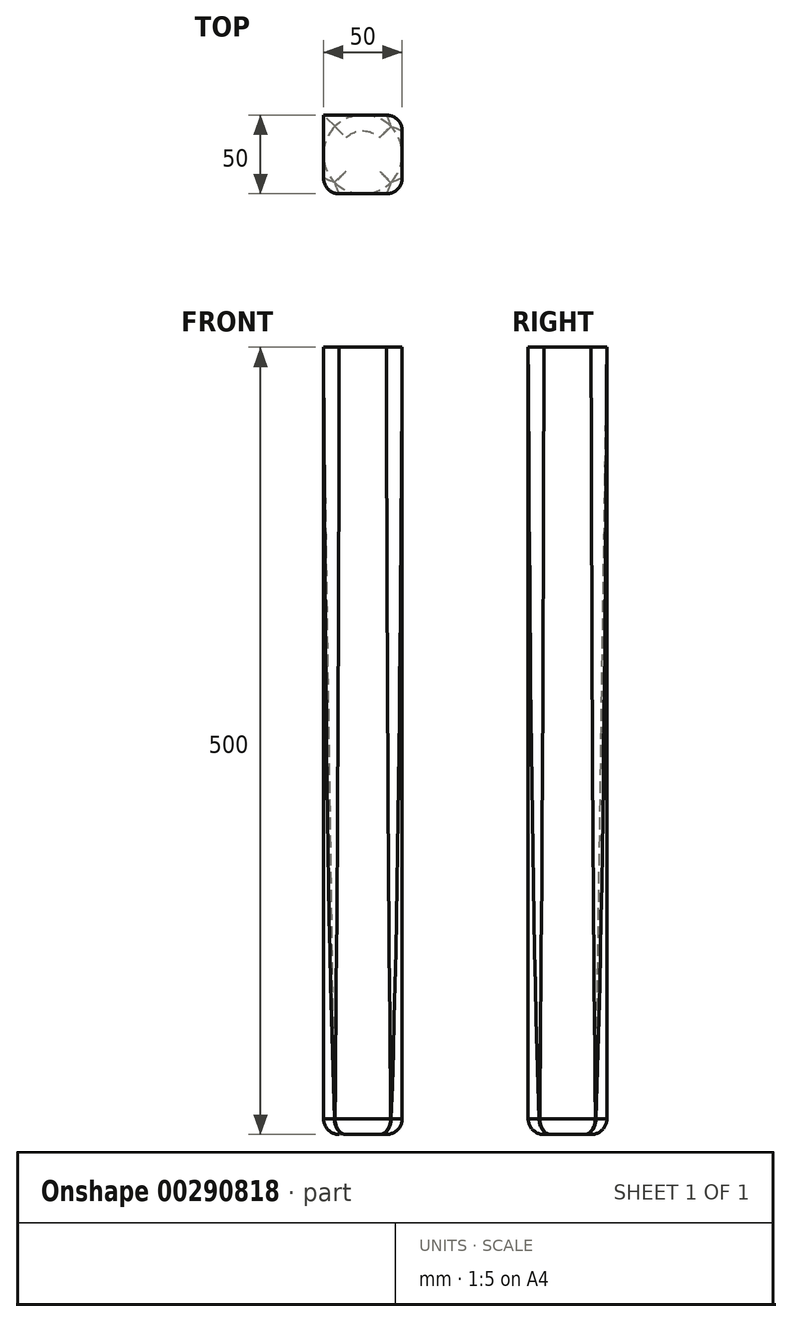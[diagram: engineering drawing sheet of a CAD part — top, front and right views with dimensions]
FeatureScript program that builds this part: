
annotation { "Feature Type Name" : "Feature", "Feature Type Description" : "" }
export const myFeature = defineFeature(function(context is Context, id is Id, definition is map)
    precondition{}
    {
        {
            var Q0;
            Q0=qCreatedBy(makeId("Top.planeOp"),FACE);
            var sketch = newSketch(context, id + "F0", { "sketchPlane" : qUnion([Q0])});
            skCircle(sketch, "E0", {"center": v(0, 0) * mm, "radius": 25 * mm});
            skSolve(sketch);
        }
        {
            var Q0;
            Q0=qCreatedBy(makeId("Top.planeOp"),FACE);
            cPlane(context, id + "F1", {"entities" : qUnion([Q0]), "cplaneType" : CPlaneType.OFFSET, "offset" : 500 * mm, "width" : 150 * mm, "height" : 150 * mm});
        }
        {
            var Q0;
            Q0=qCreatedBy(id+"F1.planeOp",FACE);
            var sketch = newSketch(context, id + "F2", { "sketchPlane" : qUnion([Q0])});
            skLineSegment(sketch, "E1.bottom", {"start": v(25, 25) * mm, "end": v(-25, 25) * mm});
            skLineSegment(sketch, "E1.top", {"start": v(25, -25) * mm, "end": v(-25, -25) * mm});
            skLineSegment(sketch, "E1.left", {"start": v(25, 25) * mm, "end": v(25, -25) * mm});
            skLineSegment(sketch, "E1.right", {"start": v(-25, 25) * mm, "end": v(-25, -25) * mm});
            skPoint(sketch, "E1.middle", {"position": v(0, 0) * mm});
            skSolve(sketch);
        }
        {
            var Q0;
            Q0=makeQuery(id+"F0.imprint","IMPRINT",FACE,{"disambiguationData":[TD([[makeQuery(id+"F0.imprint","IMPRINT",EDGE,{"derivedFrom":sQuery(id+"F0.wireOp",EDGE,"E0")}),1.0]])]});
            var Q1;
            Q1=makeQuery(id+"F2.imprint","IMPRINT",FACE,{"disambiguationData":[TD([[makeQuery(id+"F2.imprint","IMPRINT",EDGE,{"derivedFrom":sQuery(id+"F2.wireOp",EDGE,"E1.bottom")}),1.0]])]});
            loft(context, id + "F3", {"sheetProfilesArray" : [{ "sheetProfileEntities" : qUnion([Q0]) }, { "sheetProfileEntities" : qUnion([Q1]) }]});
        }
        {
            var Q0;
            Q0=makeQuery(id+"F3.opLoft","SWEPT_EDGE",EDGE,{"disambiguationData":[OSD([sQuery(id+"F0.wireOp",EDGE,"E0"),sQuery(id+"F2.wireOp",EDGE,"E1.top"),sQuery(id+"F2.wireOp",EDGE,"E1.left"),sQuery(id+"F2.wireOp",EDGE,"E1.right")])]});
            var Q1;
            Q1=makeQuery(id+"F3.opLoft","SWEPT_EDGE",EDGE,{"disambiguationData":[OSD([sQuery(id+"F0.wireOp",EDGE,"E0"),sQuery(id+"F2.wireOp",EDGE,"E1.bottom"),sQuery(id+"F2.wireOp",EDGE,"E1.top"),sQuery(id+"F2.wireOp",EDGE,"E1.right")])]});
            var Q2;
            Q2=makeQuery(id+"F3.opLoft","SWEPT_EDGE",EDGE,{"disambiguationData":[OSD([sQuery(id+"F0.wireOp",EDGE,"E0"),sQuery(id+"F2.wireOp",EDGE,"E1.bottom"),sQuery(id+"F2.wireOp",EDGE,"E1.left"),sQuery(id+"F2.wireOp",EDGE,"E1.right")])]});
            var Q3;
            Q3=makeQuery(id+"F3.opLoft","SWEPT_EDGE",EDGE,{"disambiguationData":[OSD([sQuery(id+"F2.wireOp",EDGE,"E1.bottom"),sQuery(id+"F2.wireOp",EDGE,"E1.left")])]});
            var Q4;
            Q4=makeQuery(id+"F3.opLoft","CAP_FACE",FACE,{"disambiguationData":[OSD([makeQuery(id+"F0.imprint","IMPRINT",FACE,{"disambiguationData":[TD([[makeQuery(id+"F0.imprint","IMPRINT",EDGE,{"derivedFrom":sQuery(id+"F0.wireOp",EDGE,"E0")}),1.0]])]})])],"isStart":true});
            fillet(context, id + "F4", {"entities" : qUnion([Q0, Q1, Q2, Q3, Q4]), "radius" : 10 * mm, "tangentPropagation" : true, "allowEdgeOverflow" : false});
        }
    });
